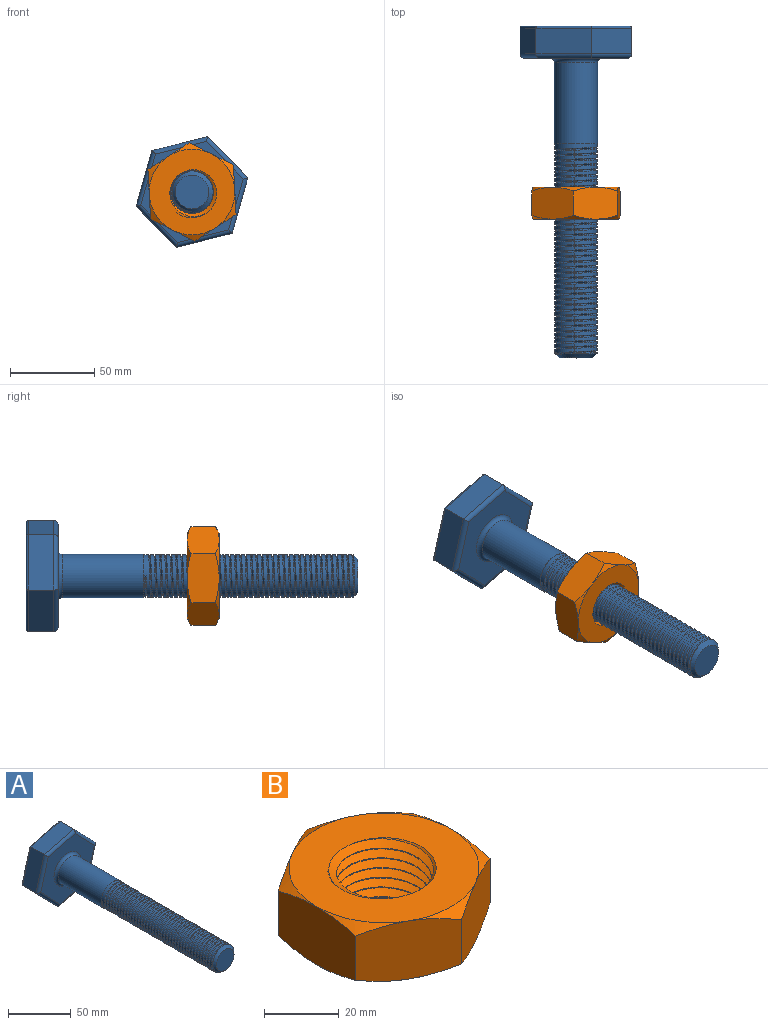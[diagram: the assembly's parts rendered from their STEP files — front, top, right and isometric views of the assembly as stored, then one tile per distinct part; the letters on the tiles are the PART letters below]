
ASSEMBLY  parts=2 mates=1
PART A: 67 faces, bbox 66.3x196.9x65.7 mm
  f0: cylinder r=12.51mm len=25.01mm, axis (0,1,0), area 267.6mm2, adj f1,f48,f51,f52,f53
  f1: cylinder r=12.51mm len=25.01mm, axis (0,1,0), area 160.6mm2, adj f0,f2,f52,f53
  f2: cylinder r=12.51mm len=25.01mm, axis (0,1,0), area 160.6mm2, adj f1,f3,f52,f53
  f3: cylinder r=12.51mm len=25.01mm, axis (0,1,0), area 160.6mm2, adj f2,f4,f52,f53
  f4: cylinder r=12.51mm len=25.01mm, axis (0,1,0), area 160.6mm2, adj f3,f5,f52,f53
  f5: cylinder r=12.51mm len=25.01mm, axis (0,1,0), area 160.6mm2, adj f4,f6,f52,f53
  f6: cylinder r=12.51mm len=25.01mm, axis (0,1,0), area 160.6mm2, adj f5,f7,f52,f53
  f7: cylinder r=12.51mm len=25.01mm, axis (0,1,0), area 160.6mm2, adj f6,f8,f52,f53
  f8: cylinder r=12.51mm len=25.01mm, axis (0,1,0), area 160.7mm2, adj f7,f9,f52,f53
  f9: cylinder r=12.51mm len=25.01mm, axis (0,1,0), area 160.6mm2, adj f8,f10,f52,f53
  f10: cylinder r=12.51mm len=25.01mm, axis (0,1,0), area 160.6mm2, adj f9,f11,f52,f53
  f11: cylinder r=12.51mm len=25.01mm, axis (0,1,0), area 160.6mm2, adj f10,f12,f52,f53
  f12: cylinder r=12.51mm len=25.01mm, axis (0,1,0), area 160.6mm2, adj f11,f13,f52,f53
  f13: cylinder r=12.51mm len=25.01mm, axis (0,1,0), area 160.6mm2, adj f12,f14,f52,f53
  f14: cylinder r=12.51mm len=25.01mm, axis (0,1,0), area 160.7mm2, adj f13,f15,f52,f53
  f15: cylinder r=12.51mm len=25.01mm, axis (0,1,0), area 160.6mm2, adj f14,f16,f52,f53
  f16: cylinder r=12.51mm len=25.01mm, axis (0,1,0), area 160.6mm2, adj f15,f17,f52,f53
  f17: cylinder r=12.51mm len=25.01mm, axis (0,1,0), area 160.6mm2, adj f16,f18,f52,f53
  f18: cylinder r=12.51mm len=25.01mm, axis (0,1,0), area 160.6mm2, adj f17,f19,f52,f53
  f19: cylinder r=12.51mm len=25.01mm, axis (0,1,0), area 160.6mm2, adj f18,f20,f52,f53
  f20: cylinder r=12.51mm len=25.01mm, axis (0,1,0), area 160.7mm2, adj f19,f21,f52,f53
  f21: cylinder r=12.51mm len=25.01mm, axis (0,1,0), area 160.7mm2, adj f20,f22,f52,f53
  f22: cylinder r=12.51mm len=25.01mm, axis (0,1,0), area 160.6mm2, adj f21,f23,f52,f53
  f23: cylinder r=12.51mm len=25.01mm, axis (0,1,0), area 160.6mm2, adj f22,f24,f52,f53
  f24: cylinder r=12.51mm len=25.01mm, axis (0,1,0), area 160.6mm2, adj f23,f25,f52,f53
  f25: cylinder r=12.51mm len=25.01mm, axis (0,1,0), area 160.6mm2, adj f24,f26,f52,f53
  f26: cylinder r=12.51mm len=25.01mm, axis (0,1,0), area 160.7mm2, adj f25,f27,f52,f53
  f27: cylinder r=12.51mm len=25.01mm, axis (0,1,0), area 160.7mm2, adj f26,f28,f52,f53
  f28: cylinder r=12.51mm len=25.01mm, axis (0,1,0), area 160.6mm2, adj f27,f29,f52,f53
  f29: cylinder r=12.51mm len=25.01mm, axis (0,1,0), area 160.6mm2, adj f28,f30,f52,f53
  f30: cylinder r=12.51mm len=25.01mm, axis (0,1,0), area 160.6mm2, adj f29,f31,f52,f53
  f31: cylinder r=12.51mm len=25.01mm, axis (0,1,0), area 160.6mm2, adj f30,f32,f52,f53
  f32: cylinder r=12.51mm len=25.01mm, axis (0,1,0), area 160.7mm2, adj f31,f33,f52,f53
  f33: cylinder r=12.51mm len=25.01mm, axis (0,1,0), area 160.7mm2, adj f32,f34,f52,f53
  f34: cylinder r=12.51mm len=25.01mm, axis (0,1,0), area 160.6mm2, adj f33,f35,f52,f53
  f35: cylinder r=12.51mm len=25.01mm, axis (0,1,0), area 160.6mm2, adj f34,f36,f52,f53
  f36: cylinder r=12.51mm len=25.01mm, axis (0,1,0), area 160.6mm2, adj f35,f37,f52,f53
  f37: cylinder r=12.51mm len=25.01mm, axis (0,1,0), area 160.6mm2, adj f36,f38,f52,f53
  f38: cylinder r=12.51mm len=25.01mm, axis (0,1,0), area 109mm2, adj f37,f50,f52,f53
  f39: plane 24.53x23.77mm, normal (-0.72,0,-0.7), area 520.5mm2, adj f40,f44,f57,f63
  f40: plane 33.13x15.24mm, normal (0.24,0,-0.97), area 520.5mm2, adj f39,f41,f55,f61
  f41: plane 32.85x15.24mm, normal (0.96,0,-0.27), area 520.5mm2, adj f40,f42,f56,f62
  f42: plane 24.53x23.77mm, normal (0.72,0,0.7), area 520.5mm2, adj f41,f43,f58,f64
  f43: plane 33.13x15.24mm, normal (-0.24,0,0.97), area 520.5mm2, adj f42,f44,f60,f66
  f44: plane 32.85x15.24mm, normal (-0.96,0,0.27), area 520.5mm2, adj f39,f43,f59,f65
  f45: plane 60.56x60.06mm, normal (0,-1,0), area 1793.4mm2, adj f54,f55,f56,f57,f58,f59,f60
  f46: plane 63.41x62.88mm, normal (0,1,0), area 2776.4mm2, adj f61,f62,f63,f64,f65,f66
  f47: cylinder r=12.8mm len=48.26mm, axis (0,1,0), area 3882.1mm2, adj f48,f54
  f48: plane 25.61x25.61mm, normal (0,-1,0), area 23.5mm2, adj f0,f47
  f49: plane 19.93x19.93mm, normal (0,-1,0), area 312.1mm2, adj f50
  f50: cone r=9.97mm half-angle=45deg, axis (0,1,0), area 234.8mm2, adj f38,f49,f52,f53
  f51: plane 1.13x0.98mm, normal (0,0,-1), area 0.6mm2, adj f0,f52,f53
  f52: bspline ~125.45x28.88mm, area 3347.8mm2, adj f0,f1,f2,f3,f4,f5,f6,f7
  f53: bspline ~125.45x28.88mm, area 3329.5mm2, adj f0,f1,f2,f3,f4,f5,f6,f7
  f54: torus R=15.34mm, axis (0,-1,0), area 344.1mm2, adj f45,f47
  f55: cylinder r=2.54mm len=33.75mm, axis (-0.97,0,-0.24), area 130.4mm2, adj f40,f45,f56,f57
  f56: cylinder r=2.54mm len=33.55mm, axis (-0.27,0,-0.96), area 130.4mm2, adj f41,f45,f55,f58
  f57: cylinder r=2.54mm len=26.29mm, axis (-0.7,0,0.72), area 130.4mm2, adj f39,f45,f55,f59
  f58: cylinder r=2.54mm len=26.29mm, axis (0.7,0,-0.72), area 130.4mm2, adj f42,f45,f56,f60
  f59: cylinder r=2.54mm len=33.55mm, axis (0.27,0,0.96), area 130.4mm2, adj f44,f45,f57,f60
  f60: cylinder r=2.54mm len=33.75mm, axis (0.97,0,0.24), area 130.4mm2, adj f43,f45,f58,f59
  f61: cylinder r=1.27mm len=33.44mm, axis (0.97,0,0.24), area 66.7mm2, adj f40,f46,f62,f63
  f62: cylinder r=1.27mm len=33.2mm, axis (0.27,0,0.96), area 66.7mm2, adj f41,f46,f61,f64
  f63: cylinder r=1.27mm len=25.41mm, axis (0.7,0,-0.72), area 66.7mm2, adj f39,f46,f61,f65
  f64: cylinder r=1.27mm len=25.41mm, axis (-0.7,0,0.72), area 66.7mm2, adj f42,f46,f62,f66
  f65: cylinder r=1.27mm len=33.2mm, axis (-0.27,0,-0.96), area 66.7mm2, adj f44,f46,f63,f66
  f66: cylinder r=1.27mm len=33.44mm, axis (-0.97,0,-0.24), area 66.7mm2, adj f43,f46,f64,f65
PART B: 24 faces, bbox 59.2x59.2x23.1 mm
  f0: plane 51.39x51.39mm, normal (0,0,1), area 1387.6mm2, adj f5,f6,f8,f10,f12,f14,f21,f22
  f1: plane 50.8x50.8mm, normal (0,0,-1), area 1421.2mm2, adj f2,f3,f4,f7,f9,f11,f13,f22
  f2: cylinder r=12.7mm len=25.4mm, axis (0,0,-1), area 112mm2, adj f1,f21,f22,f23
  f3: cone r=35.49mm half-angle=60deg, axis (0,0,1), area 40mm2, adj f1,f15,f16
  f4: cone r=35.49mm half-angle=60deg, axis (0,0,1), area 40mm2, adj f1,f15,f20
  f5: cone r=35.49mm half-angle=60deg, axis (0,0,-1), area 40mm2, adj f0,f15,f16
  f6: cone r=35.49mm half-angle=60deg, axis (0,0,-1), area 40mm2, adj f0,f15,f20
  f7: cone r=35.49mm half-angle=60deg, axis (0,0,1), area 40mm2, adj f1,f16,f17
  f8: cone r=35.49mm half-angle=60deg, axis (0,0,-1), area 40mm2, adj f0,f16,f17
  f9: cone r=35.49mm half-angle=60deg, axis (0,0,1), area 40mm2, adj f1,f17,f18
  f10: cone r=35.49mm half-angle=60deg, axis (0,0,-1), area 40mm2, adj f0,f17,f18
  f11: cone r=35.49mm half-angle=60deg, axis (0,0,1), area 40mm2, adj f1,f18,f19
  f12: cone r=35.49mm half-angle=60deg, axis (0,0,-1), area 40mm2, adj f0,f18,f19
  f13: cone r=35.49mm half-angle=60deg, axis (0,0,1), area 40mm2, adj f1,f19,f20
  f14: cone r=35.49mm half-angle=60deg, axis (0,0,-1), area 40mm2, adj f0,f19,f20
  f15: plane 25.4x19.06mm, normal (-0.5,0.87,0), area 513.1mm2, adj f3,f4,f5,f6,f16,f20
  f16: plane 25.4x19.06mm, normal (0.5,0.87,0), area 513.1mm2, adj f3,f5,f7,f8,f15,f17
  f17: plane 29.35x19.06mm, normal (1,0,0), area 513.1mm2, adj f7,f8,f9,f10,f16,f18
  f18: plane 25.4x19.06mm, normal (0.5,-0.87,0), area 513.1mm2, adj f9,f10,f11,f12,f17,f19
  f19: plane 25.4x19.06mm, normal (-0.5,-0.87,0), area 513.1mm2, adj f11,f12,f13,f14,f18,f20
  f20: plane 29.35x19.06mm, normal (-1,0,0), area 513.1mm2, adj f4,f6,f13,f14,f15,f19
  f21: cone r=12.7mm half-angle=45deg, axis (0,0,1), area 47.2mm2, adj f0,f2,f22,f23
  f22: bspline ~35.17x30.46mm, area 1513.6mm2, adj f0,f1,f2,f21,f23
  f23: bspline ~35.17x30.46mm, area 1513.5mm2, adj f0,f1,f2,f21,f22
PLACE A t=(-70.5,19.62,-57.15)mm fixed
PLACE B rot(axis=(-0.36,-0.66,-0.66),140.6deg) t=(-70.5,-94.97,-57.15)mm
MATE cylindrical B.f2 <-> A.f0  axis (0,1,0) through (-70.5,-75.92,-57.15)mm
